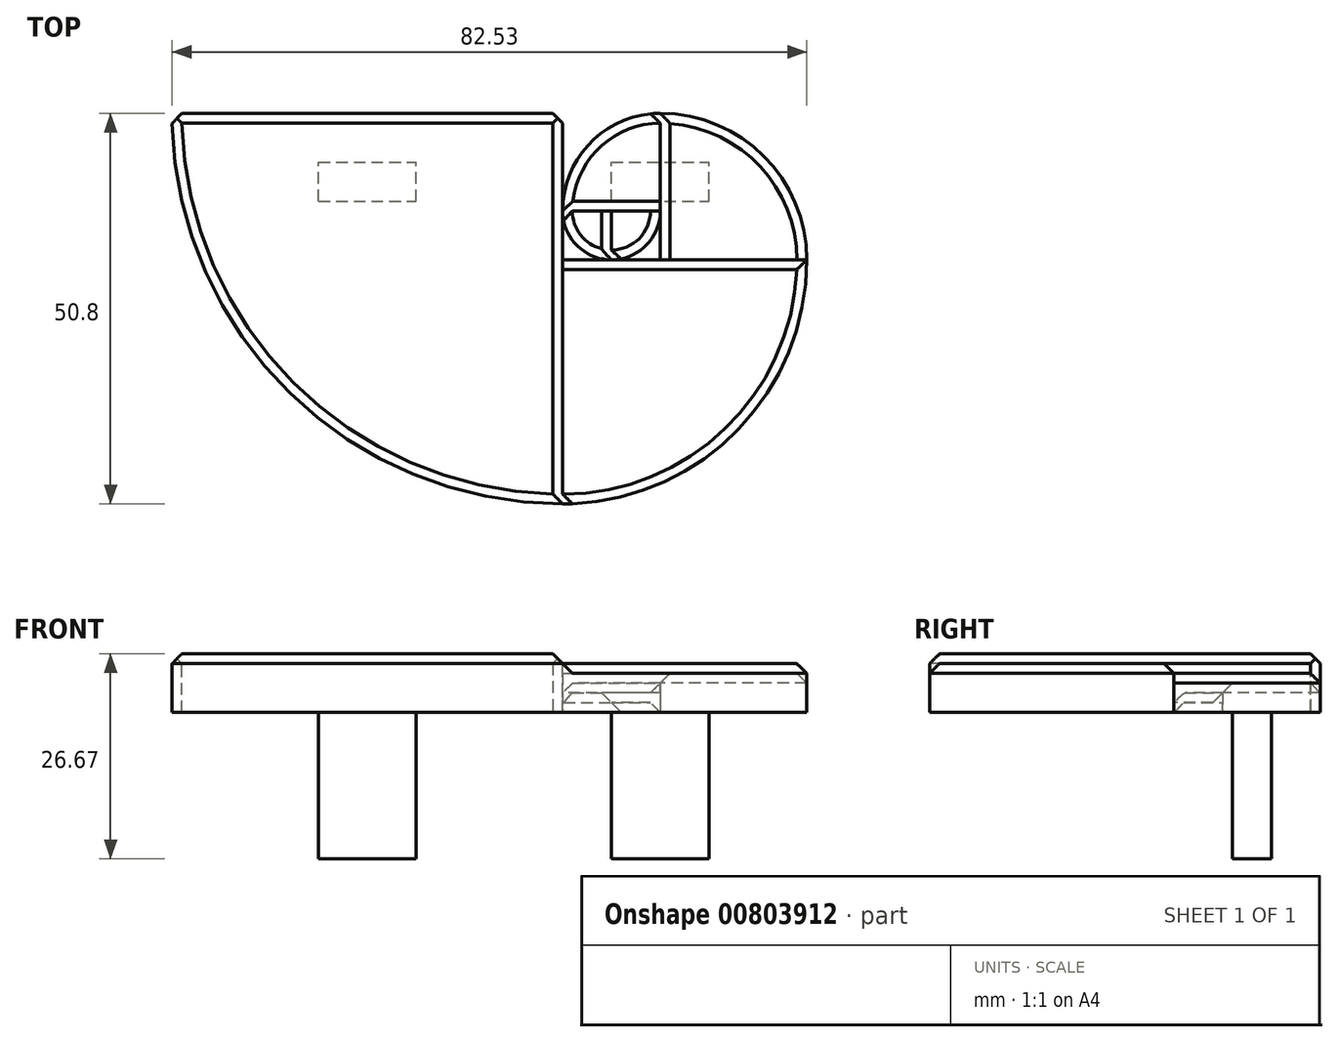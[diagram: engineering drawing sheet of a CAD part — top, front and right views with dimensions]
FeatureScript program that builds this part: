
annotation { "Feature Type Name" : "Feature", "Feature Type Description" : "" }
export const myFeature = defineFeature(function(context is Context, id is Id, definition is map)
    precondition{}
    {
        {
            var Q0;
            Q0=qCreatedBy(makeId("Top.planeOp"),FACE);
            var sketch = newSketch(context, id + "F0", { "sketchPlane" : qUnion([Q0])});
            skLineSegment(sketch, "E0.bottom", {"start": v(0, 0) * mm, "end": v(6.35, 0) * mm});
            skLineSegment(sketch, "E0.top", {"start": v(0, 6.35) * mm, "end": v(6.35, 6.35) * mm});
            skLineSegment(sketch, "E0.left", {"start": v(0, 0) * mm, "end": v(0, 6.35) * mm});
            skLineSegment(sketch, "E0.right", {"start": v(6.35, 0) * mm, "end": v(6.35, 6.35) * mm});
            skLineSegment(sketch, "E1.MirrorCS", {"start": v(12.7, 6.35) * mm, "end": v(6.35, 6.35) * mm});
            skLineSegment(sketch, "E2.MirrorCS", {"start": v(12.7, 0) * mm, "end": v(12.7, 6.35) * mm});
            skLineSegment(sketch, "E3.MirrorCS", {"start": v(12.7, 0) * mm, "end": v(6.35, 0) * mm});
            skLineSegment(sketch, "E4.bottom", {"start": v(0, 6.35) * mm, "end": v(12.7, 6.35) * mm});
            skLineSegment(sketch, "E4.top", {"start": v(0, 19.05) * mm, "end": v(12.7, 19.05) * mm});
            skLineSegment(sketch, "E4.left", {"start": v(0, 6.35) * mm, "end": v(0, 19.05) * mm});
            skLineSegment(sketch, "E4.right", {"start": v(12.7, 6.35) * mm, "end": v(12.7, 19.05) * mm});
            skLineSegment(sketch, "E5.bottom", {"start": v(12.7, 19.05) * mm, "end": v(31.75, 19.05) * mm});
            skLineSegment(sketch, "E5.top", {"start": v(12.7, 0) * mm, "end": v(31.75, 0) * mm});
            skLineSegment(sketch, "E5.left", {"start": v(12.7, 19.05) * mm, "end": v(12.7, 0) * mm});
            skLineSegment(sketch, "E5.right", {"start": v(31.75, 19.05) * mm, "end": v(31.75, 0) * mm});
            skLineSegment(sketch, "E6.bottom", {"start": v(0, 0) * mm, "end": v(31.75, 0) * mm});
            skLineSegment(sketch, "E6.top", {"start": v(0, -31.75) * mm, "end": v(31.75, -31.75) * mm});
            skLineSegment(sketch, "E6.left", {"start": v(0, 0) * mm, "end": v(0, -31.75) * mm});
            skLineSegment(sketch, "E6.right", {"start": v(31.75, 0) * mm, "end": v(31.75, -31.75) * mm});
            skLineSegment(sketch, "E7.bottom", {"start": v(0, 19.05) * mm, "end": v(-50.8, 19.05) * mm});
            skLineSegment(sketch, "E7.top", {"start": v(0, -31.75) * mm, "end": v(-50.8, -31.75) * mm});
            skLineSegment(sketch, "E7.left", {"start": v(0, 19.05) * mm, "end": v(0, -31.75) * mm});
            skLineSegment(sketch, "E7.right", {"start": v(-50.8, 19.05) * mm, "end": v(-50.8, -31.75) * mm});
            skArc(sketch, "E8", {"start": v(6.35, 0) * mm, "mid": v(10.84, 1.86) * mm, "end": v(12.7, 6.35) * mm});
            skArc(sketch, "E9.MirrorCS", {"start": v(6.35, 0) * mm, "mid": v(1.86, 1.86) * mm, "end": v(0, 6.35) * mm});
            skArc(sketch, "E10", {"start": v(12.7, 19.05) * mm, "mid": v(3.72, 15.33) * mm, "end": v(0, 6.35) * mm});
            skArc(sketch, "E11", {"start": v(31.75, 0) * mm, "mid": v(26.17, 13.47) * mm, "end": v(12.7, 19.05) * mm});
            skArc(sketch, "E12", {"start": v(0, -31.75) * mm, "mid": v(22.45, -22.45) * mm, "end": v(31.75, 0) * mm});
            skArc(sketch, "E13", {"start": v(-50.8, 19.05) * mm, "mid": v(-35.92, -16.87) * mm, "end": v(0, -31.75) * mm});
            skSolve(sketch);
        }
        {
            var Q0;
            Q0=makeQuery(id+"F0.imprint","IMPRINT",FACE,{"disambiguationData":[TD([[makeQuery(id+"F0.imprint","IMPRINT",EDGE,{"derivedFrom":sQuery(id+"F0.wireOp",EDGE,"E0.bottom")}),-1.0]])]});
            extrude(context, id + "F1", {"entities" : qUnion([Q0]), "depth" : 6.35 * mm, "offsetDistance" : 25.4 * mm});
        }
        {
            var Q0;
            Q0=makeQuery(id+"F0.imprint","IMPRINT",FACE,{"disambiguationData":[TD([[makeQuery(id+"F0.imprint","IMPRINT",EDGE,{"derivedFrom":sQuery(id+"F0.wireOp",EDGE,"E0.left")}),1.0]])]});
            extrude(context, id + "F2", {"entities" : qUnion([Q0]), "depth" : 7.62 * mm, "offsetDistance" : 25.4 * mm});
        }
        {
            var Q0;
            Q0=makeQuery(id+"F2.opExtrude","CAP_EDGE",EDGE,{"disambiguationData":[OSD([sQuery(id+"F0.wireOp",EDGE,"E0.left"),sQuery(id+"F0.wireOp",EDGE,"E4.left"),sQuery(id+"F0.wireOp",EDGE,"E6.left")])],"isStart":false});
            chamfer(context, id + "F3", {"entities" : qUnion([Q0]), "width" : 1.27 * mm, "tangentPropagation" : true});
        }
        {
            var Q0;
            Q0=makeQuery(id+"F1.opExtrude","CAP_EDGE",EDGE,{"disambiguationData":[OSD([sQuery(id+"F0.wireOp",EDGE,"E0.bottom"),sQuery(id+"F0.wireOp",EDGE,"E3.MirrorCS"),sQuery(id+"F0.wireOp",EDGE,"E5.top")])],"isStart":false});
            chamfer(context, id + "F4", {"entities" : qUnion([Q0]), "width" : 1.27 * mm, "tangentPropagation" : true});
        }
        {
            var Q0;
            Q0=makeQuery(id+"F0.imprint","IMPRINT",FACE,{"disambiguationData":[TD([[makeQuery(id+"F0.imprint","IMPRINT",EDGE,{"derivedFrom":sQuery(id+"F0.wireOp",EDGE,"E0.right")}),-1.0]])]});
            extrude(context, id + "F5", {"entities" : qUnion([Q0]), "depth" : 1.27 * mm, "offsetDistance" : 25.4 * mm});
        }
        {
            var Q0;
            Q0=makeQuery(id+"F0.imprint","IMPRINT",FACE,{"disambiguationData":[TD([[makeQuery(id+"F0.imprint","IMPRINT",EDGE,{"derivedFrom":sQuery(id+"F0.wireOp",EDGE,"E0.top")}),-1.0]])]});
            extrude(context, id + "F6", {"entities" : qUnion([Q0]), "operationType" : NewBodyOperationType.ADD, "depth" : 2.54 * mm, "offsetDistance" : 25.4 * mm});
        }
        {
            var Q0;
            Q0=makeQuery(id+"F0.imprint","IMPRINT",FACE,{"disambiguationData":[TD([[makeQuery(id+"F0.imprint","IMPRINT",EDGE,{"derivedFrom":sQuery(id+"F0.wireOp",EDGE,"E0.top")}),1.0]])]});
            extrude(context, id + "F7", {"entities" : qUnion([Q0]), "operationType" : NewBodyOperationType.ADD, "depth" : 3.8 * mm, "offsetDistance" : 25.4 * mm});
        }
        {
            var Q0;
            Q0=makeQuery(id+"F0.imprint","IMPRINT",FACE,{"disambiguationData":[TD([[makeQuery(id+"F0.imprint","IMPRINT",EDGE,{"derivedFrom":sQuery(id+"F0.wireOp",EDGE,"E2.MirrorCS")}),-1.0]])]});
            extrude(context, id + "F8", {"entities" : qUnion([Q0]), "depth" : 5.08 * mm, "offsetDistance" : 25.4 * mm});
        }
        {
            var Q0;
            Q0=makeQuery(id+"F5.opExtrude","SWEPT_BODY",BODY,{"disambiguationData":[OSD([sQuery(id+"F0.wireOp",EDGE,"E0.right"),sQuery(id+"F0.wireOp",EDGE,"E1.MirrorCS"),sQuery(id+"F0.wireOp",EDGE,"E8")])]});
            var Q1;
            Q1=makeQuery(id+"F8.opExtrude","SWEPT_BODY",BODY,{"disambiguationData":[OSD([sQuery(id+"F0.wireOp",EDGE,"E2.MirrorCS"),sQuery(id+"F0.wireOp",EDGE,"E4.right"),sQuery(id+"F0.wireOp",EDGE,"E5.top"),sQuery(id+"F0.wireOp",EDGE,"E11")])]});
            booleanBodies(context, id + "F9", {"operationType" : BooleanOperationType.UNION, "tools" : qUnion([Q0, Q1])});
        }
        {
            var Q0;
            Q0=makeQuery(id+"F8.opExtrude","CAP_EDGE",EDGE,{"disambiguationData":[OSD([sQuery(id+"F0.wireOp",EDGE,"E2.MirrorCS"),sQuery(id+"F0.wireOp",EDGE,"E4.right")])],"isStart":false});
            chamfer(context, id + "F10", {"entities" : qUnion([Q0]), "width" : 1.27 * mm, "tangentPropagation" : true});
        }
        {
            var Q0;
            Q0=makeQuery(id+"F7.opExtrude","CAP_EDGE",EDGE,{"disambiguationData":[OSD([sQuery(id+"F0.wireOp",EDGE,"E0.top"),sQuery(id+"F0.wireOp",EDGE,"E1.MirrorCS")])],"isStart":false});
            chamfer(context, id + "F11", {"entities" : qUnion([Q0]), "width" : 1.27 * mm, "tangentPropagation" : true});
        }
        {
            var Q0;
            Q0=makeQuery(id+"F6.opExtrude","CAP_EDGE",EDGE,{"disambiguationData":[OSD([sQuery(id+"F0.wireOp",EDGE,"E0.right")])],"isStart":false});
            chamfer(context, id + "F12", {"entities" : qUnion([Q0]), "width" : 1.27 * mm, "tangentPropagation" : true});
        }
        {
            var Q0;
            Q0=makeQuery(id+"F2.opExtrude","CAP_EDGE",EDGE,{"disambiguationData":[OSD([sQuery(id+"F0.wireOp",EDGE,"E7.bottom")])],"isStart":false});
            var Q1;
            Q1=makeQuery(id+"F2.opExtrude","SWEPT_EDGE",EDGE,{"disambiguationData":[OSD([sQuery(id+"F0.wireOp",EDGE,"E4.top"),sQuery(id+"F0.wireOp",EDGE,"E4.left"),sQuery(id+"F0.wireOp",EDGE,"E7.bottom")])]});
            var Q2;
            Q2=makeQuery(id+"F2.opExtrude","SWEPT_EDGE",EDGE,{"disambiguationData":[OSD([sQuery(id+"F0.wireOp",EDGE,"E7.bottom"),sQuery(id+"F0.wireOp",EDGE,"E7.right"),sQuery(id+"F0.wireOp",EDGE,"E13")])]});
            chamfer(context, id + "F13", {"entities" : qUnion([Q0, Q1, Q2]), "width" : 1.27 * mm, "tangentPropagation" : true});
        }
        {
            var Q0;
            Q0=makeQuery(id+"F2.opExtrude","CAP_EDGE",EDGE,{"disambiguationData":[OSD([sQuery(id+"F0.wireOp",EDGE,"E13")])],"isStart":false});
            chamfer(context, id + "F14", {"entities" : qUnion([Q0]), "width" : 1.27 * mm, "tangentPropagation" : true});
        }
        {
            var Q0;
            Q0=makeQuery(id+"F1.opExtrude","CAP_EDGE",EDGE,{"disambiguationData":[OSD([sQuery(id+"F0.wireOp",EDGE,"E12")])],"isStart":false});
            chamfer(context, id + "F15", {"entities" : qUnion([Q0]), "width" : 1.27 * mm, "tangentPropagation" : true});
        }
        {
            var Q0;
            Q0=makeQuery(id+"F8.opExtrude","CAP_EDGE",EDGE,{"disambiguationData":[OSD([sQuery(id+"F0.wireOp",EDGE,"E11")])],"isStart":false});
            chamfer(context, id + "F16", {"entities" : qUnion([Q0]), "width" : 1.27 * mm, "tangentPropagation" : true});
        }
        {
            var Q0;
            Q0=makeQuery(id+"F7.opExtrude","CAP_EDGE",EDGE,{"disambiguationData":[OSD([sQuery(id+"F0.wireOp",EDGE,"E10")])],"isStart":false});
            chamfer(context, id + "F17", {"entities" : qUnion([Q0]), "width" : 1.27 * mm, "tangentPropagation" : true});
        }
        {
            var Q0;
            Q0=makeQuery(id+"F6.opExtrude","CAP_EDGE",EDGE,{"disambiguationData":[OSD([sQuery(id+"F0.wireOp",EDGE,"E9.MirrorCS")])],"isStart":false});
            chamfer(context, id + "F18", {"entities" : qUnion([Q0]), "width" : 1.27 * mm, "tangentPropagation" : true});
        }
        {
            var Q0;
            Q0=makeQuery(id+"F5.opExtrude","CAP_EDGE",EDGE,{"disambiguationData":[OSD([sQuery(id+"F0.wireOp",EDGE,"E8")])],"isStart":false});
            chamfer(context, id + "F19", {"entities" : qUnion([Q0]), "width" : 1.27 * mm, "tangentPropagation" : true});
        }
        {
            var Q0;
            {var subQ0=sQuery(id+"F0.wireOp",EDGE,"E4.right");var subQ1=sQuery(id+"F0.wireOp",EDGE,"E1.MirrorCS");var subQ2=sQuery(id+"F0.wireOp",EDGE,"E0.top");var subQ3=sQuery(id+"F0.wireOp",EDGE,"E0.right");Q0=makeQuery(id+"F9.opBoolean","MERGE",FACE,{"derivedFrom":[makeQuery(id+"F7.boolean.opBoolean","MERGE",FACE,{"derivedFrom":[makeQuery(id+"F6.boolean.opBoolean","MERGE",FACE,{"derivedFrom":[makeQuery(id+"F5.opExtrude","CAP_FACE",FACE,{"disambiguationData":[OSD([subQ3,subQ1,sQuery(id+"F0.wireOp",EDGE,"E8")])],"isStart":true}),makeQuery(id+"F6.opExtrude","CAP_FACE",FACE,{"disambiguationData":[OSD([subQ2,subQ3,sQuery(id+"F0.wireOp",EDGE,"E9.MirrorCS")])],"isStart":true})]}),makeQuery(id+"F7.opExtrude","CAP_FACE",FACE,{"disambiguationData":[OSD([subQ2,subQ1,subQ0,sQuery(id+"F0.wireOp",EDGE,"E10")])],"isStart":true})]}),makeQuery(id+"F8.opExtrude","CAP_FACE",FACE,{"disambiguationData":[OSD([sQuery(id+"F0.wireOp",EDGE,"E2.MirrorCS"),subQ0,sQuery(id+"F0.wireOp",EDGE,"E5.top"),sQuery(id+"F0.wireOp",EDGE,"E11")])],"isStart":true})]});}
            var sketch = newSketch(context, id + "F20", { "sketchPlane" : qUnion([Q0])});
            skLineSegment(sketch, "E14.bottom", {"start": v(6.35, -7.62) * mm, "end": v(19.05, -7.62) * mm});
            skLineSegment(sketch, "E14.top", {"start": v(6.35, -12.7) * mm, "end": v(19.05, -12.7) * mm});
            skLineSegment(sketch, "E14.left", {"start": v(6.35, -7.62) * mm, "end": v(6.35, -12.7) * mm});
            skLineSegment(sketch, "E14.right", {"start": v(19.05, -7.62) * mm, "end": v(19.05, -12.7) * mm});
            skPoint(sketch, "E14.middle", {"position": v(12.7, -10.16) * mm});
            skLineSegment(sketch, "E15.MirrorCS", {"start": v(-12.7, -3.8) * mm, "end": v(-12.7, -16.5) * mm, "construction": true});
            skLineSegment(sketch, "E16.MirrorCS", {"start": v(-38.1, -3.8) * mm, "end": v(-38.1, -16.51) * mm, "construction": true});
            skLineSegment(sketch, "E17", {"start": v(-38.1, -3.8) * mm, "end": v(-12.7, -3.8) * mm, "construction": true});
            skLineSegment(sketch, "E18", {"start": v(-12.7, -10.16) * mm, "end": v(-38.1, -10.16) * mm, "construction": true});
            skLineSegment(sketch, "E19.bottom", {"start": v(-31.75, -7.62) * mm, "end": v(-19.05, -7.62) * mm});
            skLineSegment(sketch, "E19.top", {"start": v(-31.75, -12.7) * mm, "end": v(-19.05, -12.7) * mm});
            skLineSegment(sketch, "E19.left", {"start": v(-31.75, -7.62) * mm, "end": v(-31.75, -12.7) * mm});
            skLineSegment(sketch, "E19.right", {"start": v(-19.05, -7.62) * mm, "end": v(-19.05, -12.7) * mm});
            skPoint(sketch, "E19.middle", {"position": v(-25.4, -10.16) * mm});
            skLineSegment(sketch, "E20", {"start": v(-25.4, -10.16) * mm, "end": v(12.7, -10.16) * mm, "construction": true});
            skLineSegment(sketch, "E21", {"start": v(-19.05, -7.62) * mm, "end": v(6.35, -7.62) * mm, "construction": true});
            skLineSegment(sketch, "E22", {"start": v(-19.05, -12.7) * mm, "end": v(6.35, -12.7) * mm, "construction": true});
            skSolve(sketch);
        }
        {
            var Q0;
            Q0=makeQuery(id+"F20.imprint","IMPRINT",FACE,{"disambiguationData":[TD([[makeQuery(id+"F20.imprint","IMPRINT",EDGE,{"derivedFrom":sQuery(id+"F20.wireOp",EDGE,"E19.bottom")}),-1.0]])]});
            var Q1;
            Q1=makeQuery(id+"F20.imprint","IMPRINT",FACE,{"disambiguationData":[TD([[makeQuery(id+"F20.imprint","IMPRINT",EDGE,{"derivedFrom":sQuery(id+"F20.wireOp",EDGE,"E14.bottom")}),-1.0]])]});
            extrude(context, id + "F21", {"entities" : qUnion([Q0, Q1]), "depth" : 19.05 * mm, "offsetDistance" : 25.4 * mm});
        }
    });
